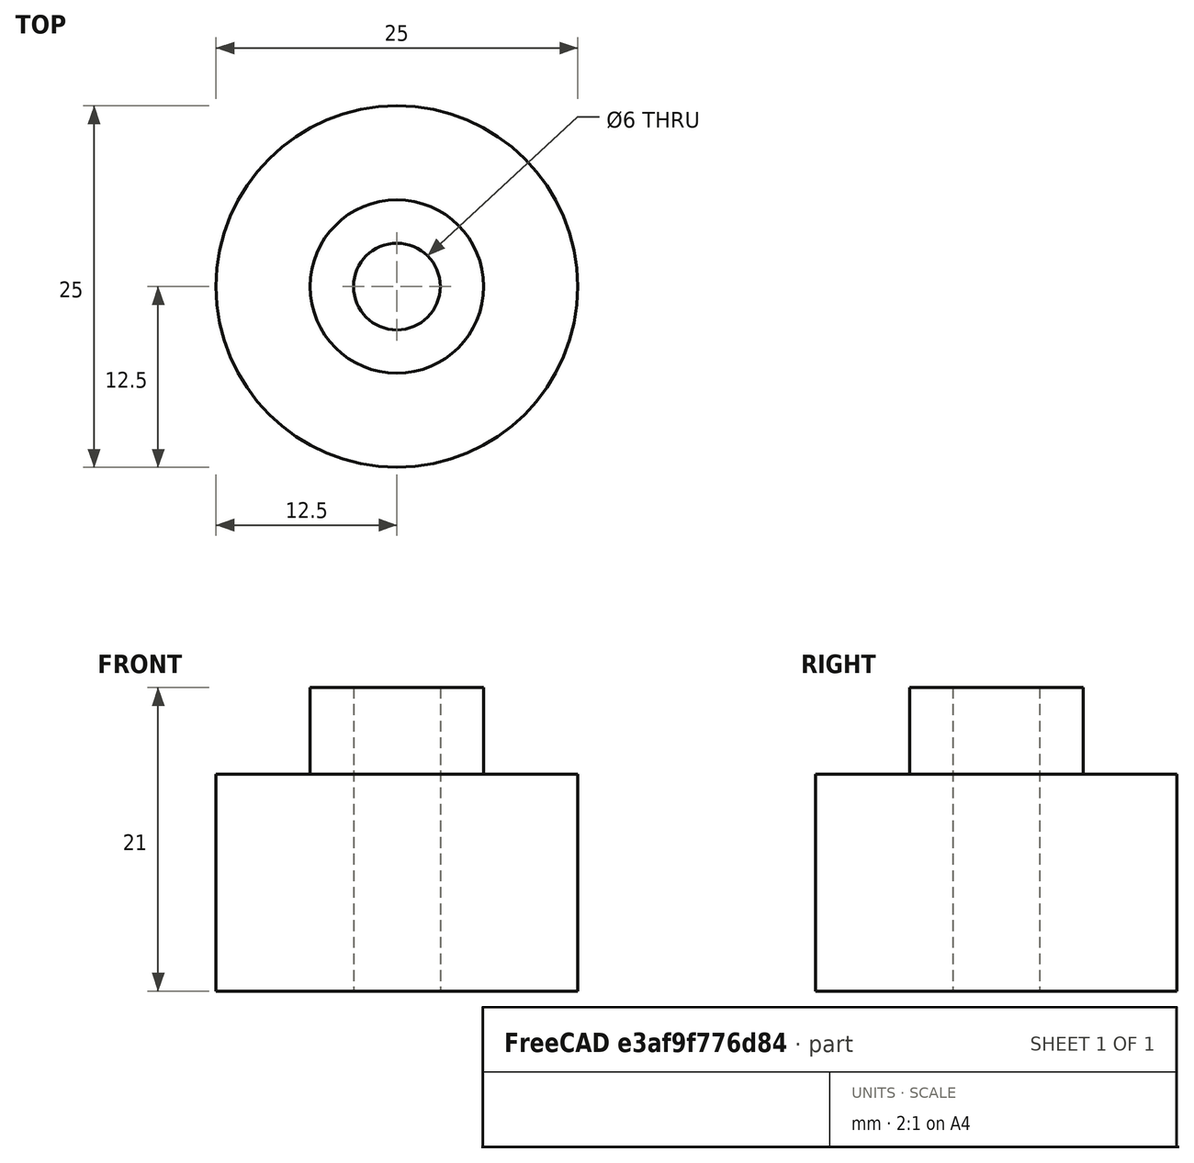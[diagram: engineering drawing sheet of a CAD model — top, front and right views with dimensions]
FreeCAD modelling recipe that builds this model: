
FCSTD DOCUMENT  (FreeCAD 0.18R16110 (Git))
Label: pulley_xy
License: All rights reserved
LicenseURL: http://en.wikipedia.org/wiki/All_rights_reserved
objects: Sketcher::SketchObject×1, PartDesign::Revolution×1, PartDesign::Body×1
note: 4 computed .brp shape members not serialized (recipe doc carries the construction recipe); baked Part::Feature solids carry a one-line shape summary decoded from their .brp

FEATURE [Sketcher::SketchObject] Sketch
  MapMode = 5
  Placement = pos=(0,0,0) rot=(1,0,0;1.5708rad)
  Support = -> [XZ_Plane]
  sketch-geometry (6):
    g0: LineSegment StartX=3 StartY=0 StartZ=0 EndX=12.5 EndY=0 EndZ=0
    g1: LineSegment StartX=12.5 StartY=0 StartZ=0 EndX=12.5 EndY=15 EndZ=0
    g2: LineSegment StartX=12.5 StartY=15 StartZ=0 EndX=6 EndY=15 EndZ=0
    g3: LineSegment StartX=6 StartY=15 StartZ=0 EndX=6 EndY=21 EndZ=0
    g4: LineSegment StartX=6 StartY=21 StartZ=0 EndX=3 EndY=21 EndZ=0
    g5: LineSegment StartX=3 StartY=21 StartZ=0 EndX=3 EndY=0 EndZ=0
  constraints (18):
    c: Coincident(g0,g1)
    c: Coincident(g1,g2)
    c: Coincident(g2,g3)
    c: Coincident(g3,g4)
    c: Coincident(g4,g5)
    c: Coincident(g5,g0)
    c: Vertical(g5)
    c: Vertical(g3)
    c: Vertical(g1)
    c: Horizontal(g4)
    c: Horizontal(g2)
    c: Horizontal(g0)
    c: PointOnObject(g0,g-1)
    c: DistanceX(g-1,g0) = 12.5
    c: DistanceX(g-1,g3) = 6
    c: DistanceX(g-1,g4) = 3
    c: DistanceY(g5,g5) = 21
    c: DistanceY(g1,g1) = 15
FEATURE [PartDesign::Revolution] Revolution
  Angle = 360
  Axis = (0,2e-16,1)
  Base = (0,0,0)
  Placement = pos=(0,0,0) rot=(1,0,0;1.5708rad)
  Profile = -> Sketch
  ReferenceAxis = -> Sketch [V_Axis]
  Reversed = true
FEATURE [PartDesign::Body] Body
  Group = -> [Sketch,Revolution]
  Origin = -> Origin
  Tip = -> Revolution
